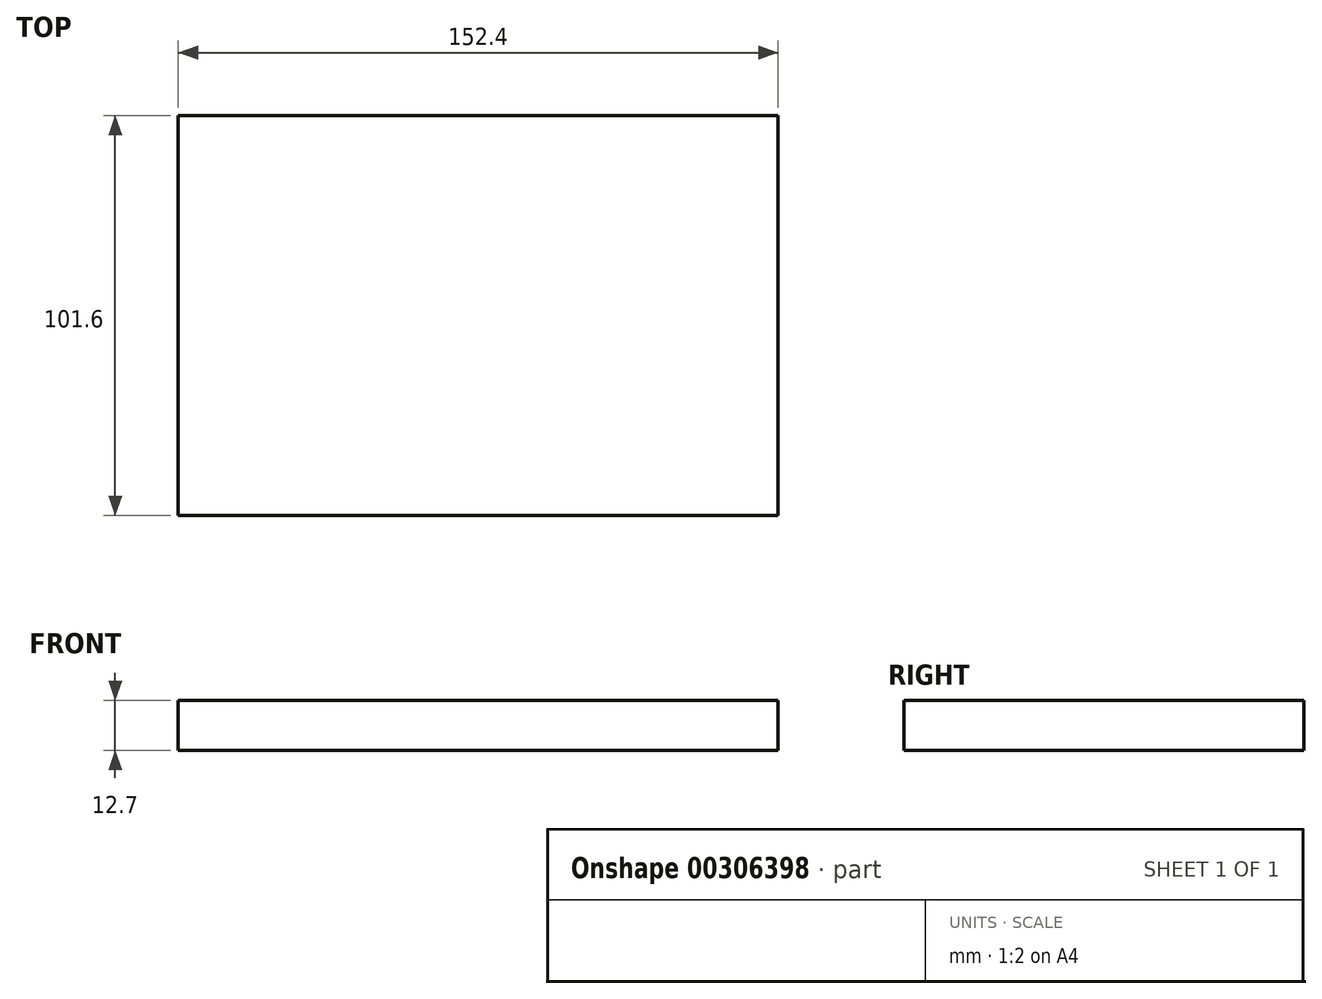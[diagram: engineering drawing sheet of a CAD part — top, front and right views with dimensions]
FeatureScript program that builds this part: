
annotation { "Feature Type Name" : "Feature", "Feature Type Description" : "" }
export const myFeature = defineFeature(function(context is Context, id is Id, definition is map)
    precondition{}
    {
        {
            var Q0;
            Q0=qCreatedBy(makeId("Top.planeOp"),FACE);
            var sketch = newSketch(context, id + "F0", { "sketchPlane" : qUnion([Q0])});
            skPoint(sketch, "E0.middle", {"position": v(0, 0) * mm});
            skLineSegment(sketch, "E1.bottom", {"start": v(76.2, -50.8) * mm, "end": v(-76.2, -50.8) * mm});
            skLineSegment(sketch, "E1.top", {"start": v(76.2, 50.8) * mm, "end": v(-76.2, 50.8) * mm});
            skLineSegment(sketch, "E1.left", {"start": v(76.2, -50.8) * mm, "end": v(76.2, 50.8) * mm});
            skLineSegment(sketch, "E1.right", {"start": v(-76.2, -50.8) * mm, "end": v(-76.2, 50.8) * mm});
            skSolve(sketch);
        }
        {
            var Q0;
            Q0 = qSketchRegion(id + "F0", true);
            extrude(context, id + "F1", {"entities" : qUnion([Q0]), "depth" : 12.7 * mm});
        }
    });
